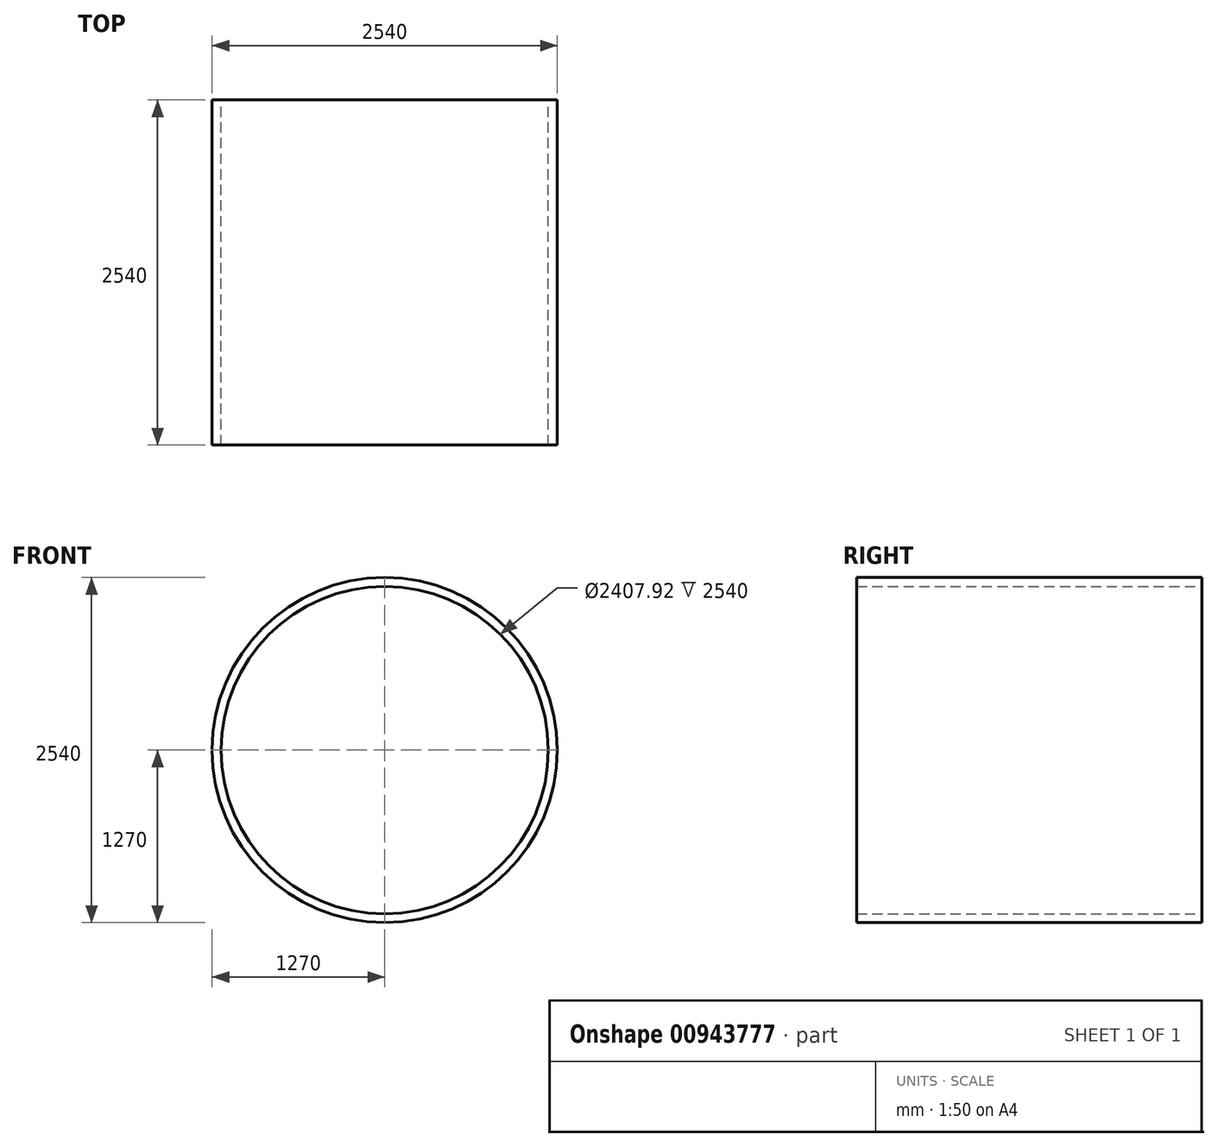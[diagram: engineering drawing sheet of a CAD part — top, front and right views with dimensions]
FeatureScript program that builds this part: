
annotation { "Feature Type Name" : "Feature", "Feature Type Description" : "" }
export const myFeature = defineFeature(function(context is Context, id is Id, definition is map)
    precondition{}
    {
        {
            var Q0;
            Q0=qCreatedBy(makeId("Front.planeOp"),FACE);
            var sketch = newSketch(context, id + "F0", { "sketchPlane" : qUnion([Q0])});
            skCircle(sketch, "E0", {"center": v(0, 0) * mm, "radius": 1270 * mm});
            skCircle(sketch, "E1", {"center": v(0, 0) * mm, "radius": 1203.96 * mm});
            skSolve(sketch);
        }
        {
            var Q0;
            Q0=makeQuery(id+"F0.imprint","IMPRINT",FACE,{"disambiguationData":[TD([[makeQuery(id+"F0.imprint","IMPRINT",EDGE,{"derivedFrom":sQuery(id+"F0.wireOp",EDGE,"E0")}),1.0]])]});
            extrude(context, id + "F1", {"entities" : qUnion([Q0]), "depth" : 2540 * mm, "offsetDistance" : 25.4 * mm});
        }
    });
